FCSTD DOCUMENT  (FreeCAD 1.0R39319 (Git))
Label: two_wires_open
License: All rights reserved
LicenseURL: http://en.wikipedia.org/wiki/All_rights_reserved
objects: App::DocumentObjectGroupPython×3, Part::Part2DObjectPython×2, App::FeaturePython×1
note: 2 computed .brp shape members not serialized (recipe doc carries the construction recipe); baked Part::Feature solids carry a one-line shape summary decoded from their .brp

FEATURE [App::FeaturePython] PECMaterial  label="PEC"  # WARN: FeaturePython — macro-defined, semantics opaque (R4)
FEATURE [Part::Part2DObjectPython] Circle001  label="Conductor_0"  # Draft 2D object (typed FeaturePython)
  Area = 12.5664
  FirstAngle = 0
  LastAngle = 0
  MakeFace = true
  Material = -> PECMaterial
  Placement = pos=(-25,0,0) rot=(0,0,1;0rad)
  Radius = 2
FEATURE [Part::Part2DObjectPython] Circle002  label="Conductor_1"  # Draft 2D object (typed FeaturePython)
  Area = 12.5664
  FirstAngle = 0
  LastAngle = 0
  MakeFace = true
  Material = -> PECMaterial
  Placement = pos=(25,0,0) rot=(0,0,1;0rad)
  Radius = 2
FEATURE [App::DocumentObjectGroupPython] MaterialGroup  label="Materials"  # scripted group (container) (typed FeaturePython)
  Group = -> [PECMaterial]
FEATURE [App::DocumentObjectGroupPython] CaseStudy  label="Model"  # scripted group (container) (typed FeaturePython)
  Group = -> [Circle002,Circle001]
FEATURE [App::DocumentObjectGroupPython] CrossSection  label="Cross-Section"  # scripted group (container) (typed FeaturePython)
  Group = -> [MaterialGroup,CaseStudy]
